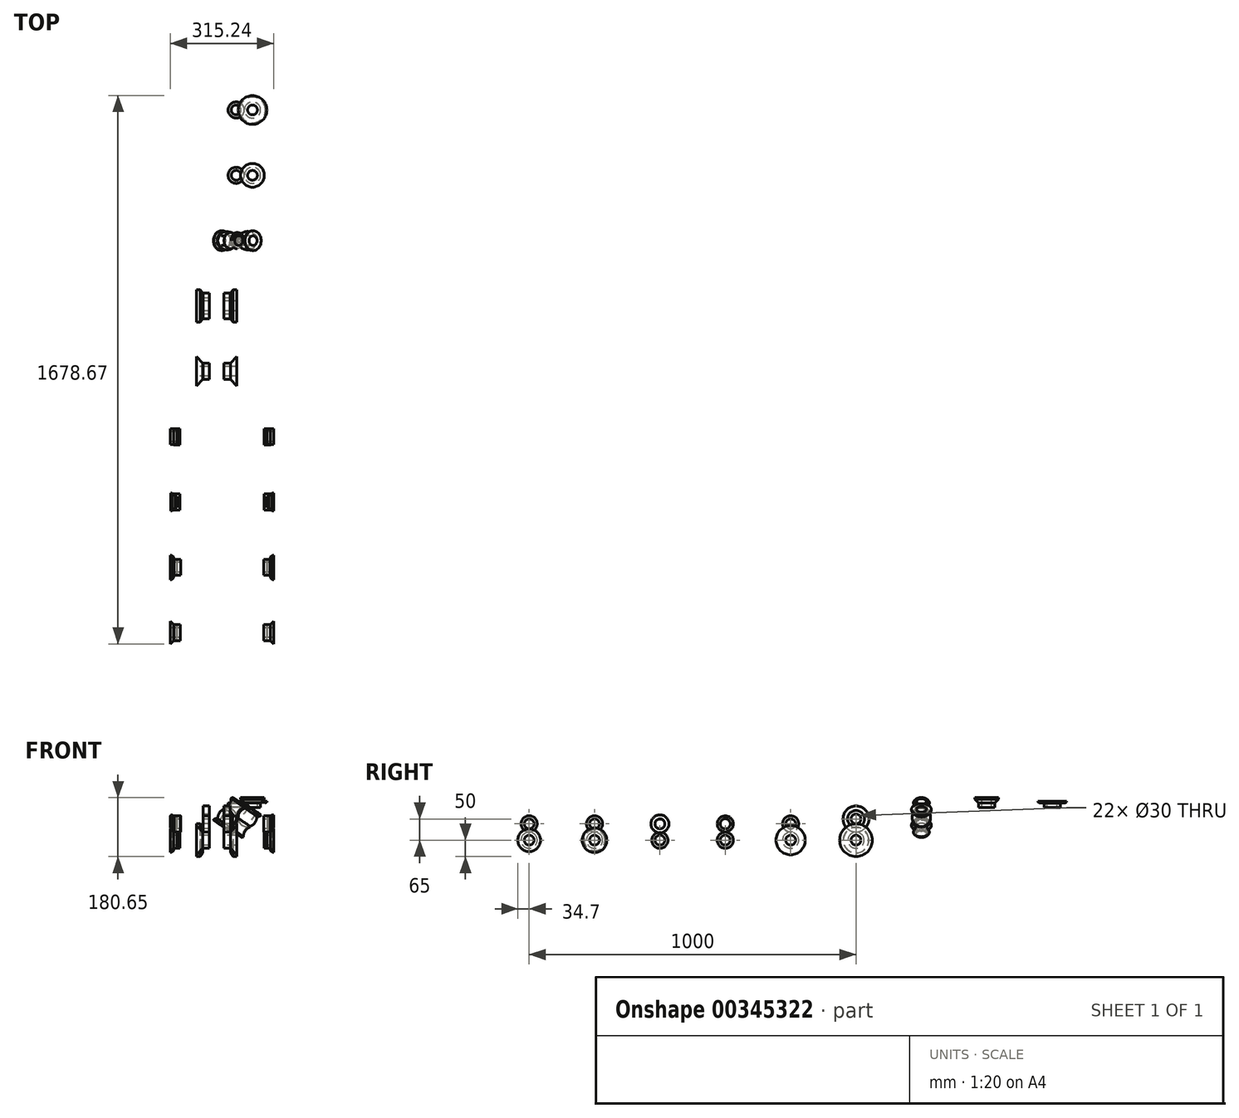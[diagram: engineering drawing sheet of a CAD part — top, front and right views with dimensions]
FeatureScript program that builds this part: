
annotation { "Feature Type Name" : "Feature", "Feature Type Description" : "" }
export const myFeature = defineFeature(function(context is Context, id is Id, definition is map)
    precondition{}
    {
        {
            var Q0;
            Q0=qCreatedBy(makeId("Front.planeOp"),FACE);
            var sketch = newSketch(context, id + "F0", { "sketchPlane" : qUnion([Q0])});
            skLineSegment(sketch, "E0", {"start": v(0, 0) * mm, "end": v(0, 89) * mm});
            skLineSegment(sketch, "E1", {"start": v(0, 0) * mm, "end": v(84, 0) * mm});
            skLineSegment(sketch, "E2", {"start": v(84, 0) * mm, "end": v(84, 14) * mm});
            skLineSegment(sketch, "E3", {"start": v(84, 14) * mm, "end": v(127, 75) * mm, "construction": true});
            skLineSegment(sketch, "E4", {"start": v(127, 75) * mm, "end": v(127, 89) * mm});
            skLineSegment(sketch, "E5", {"start": v(127, 89) * mm, "end": v(113, 89) * mm});
            skArc(sketch, "E6", {"start": v(84, 14) * mm, "mid": v(100.07, 25.5) * mm, "end": v(105.5, 44.5) * mm});
            skArc(sketch, "E7", {"start": v(127, 75) * mm, "mid": v(110.93, 63.5) * mm, "end": v(105.5, 44.5) * mm});
            skLineSegment(sketch, "E8", {"start": v(0, 89) * mm, "end": v(2, 89) * mm});
            skLineSegment(sketch, "E9", {"start": v(2, 89) * mm, "end": v(2, 83) * mm});
            skLineSegment(sketch, "E10", {"start": v(113, 89) * mm, "end": v(113, 87) * mm});
            skLineSegment(sketch, "E11", {"start": v(113, 87) * mm, "end": v(119, 87) * mm});
            skSolve(sketch);
        }
        {
            var Q0;
            Q0=qCreatedBy(makeId("Front.planeOp"),FACE);
            cPlane(context, id + "F1", {"entities" : qUnion([Q0]), "cplaneType" : CPlaneType.OFFSET, "offset" : 200 * mm, "oppositeDirection" : true, "width" : 150 * mm, "height" : 150 * mm});
        }
        {
            var Q0;
            Q0=qCreatedBy(id+"F1.planeOp",FACE);
            cPlane(context, id + "F2", {"entities" : qUnion([Q0]), "cplaneType" : CPlaneType.OFFSET, "offset" : 200 * mm, "oppositeDirection" : true, "width" : 150 * mm, "height" : 150 * mm});
        }
        {
            var Q0;
            Q0=qCreatedBy(id+"F2.planeOp",FACE);
            cPlane(context, id + "F3", {"entities" : qUnion([Q0]), "cplaneType" : CPlaneType.OFFSET, "offset" : 200 * mm, "oppositeDirection" : true, "width" : 150 * mm, "height" : 150 * mm});
        }
        {
            var Q0;
            Q0=qCreatedBy(id+"F3.planeOp",FACE);
            cPlane(context, id + "F4", {"entities" : qUnion([Q0]), "cplaneType" : CPlaneType.OFFSET, "offset" : 200 * mm, "oppositeDirection" : true, "width" : 150 * mm, "height" : 150 * mm});
        }
        {
            var Q0;
            Q0=qCreatedBy(id+"F4.planeOp",FACE);
            cPlane(context, id + "F5", {"entities" : qUnion([Q0]), "cplaneType" : CPlaneType.OFFSET, "offset" : 200 * mm, "oppositeDirection" : true, "width" : 150 * mm, "height" : 150 * mm});
        }
        {
            var Q0;
            Q0=qCreatedBy(id+"F5.planeOp",FACE);
            cPlane(context, id + "F6", {"entities" : qUnion([Q0]), "cplaneType" : CPlaneType.OFFSET, "offset" : 200 * mm, "oppositeDirection" : true, "width" : 150 * mm, "height" : 150 * mm});
        }
        {
            var Q0;
            Q0=qCreatedBy(id+"F6.planeOp",FACE);
            cPlane(context, id + "F7", {"entities" : qUnion([Q0]), "cplaneType" : CPlaneType.OFFSET, "offset" : 200 * mm, "oppositeDirection" : true, "width" : 150 * mm, "height" : 150 * mm});
        }
        {
            var Q0;
            Q0=qCreatedBy(id+"F7.planeOp",FACE);
            cPlane(context, id + "F8", {"entities" : qUnion([Q0]), "cplaneType" : CPlaneType.OFFSET, "offset" : 200 * mm, "oppositeDirection" : true, "width" : 150 * mm, "height" : 150 * mm});
        }
        {
            var Q0;
            Q0=qCreatedBy(id+"F8.planeOp",FACE);
            cPlane(context, id + "F9", {"entities" : qUnion([Q0]), "cplaneType" : CPlaneType.OFFSET, "offset" : 200 * mm, "oppositeDirection" : true, "width" : 150 * mm, "height" : 150 * mm});
        }
        {
            var Q0;
            Q0=qCreatedBy(id+"F9.planeOp",FACE);
            cPlane(context, id + "F10", {"entities" : qUnion([Q0]), "cplaneType" : CPlaneType.OFFSET, "offset" : 200 * mm, "oppositeDirection" : true, "width" : 150 * mm, "height" : 150 * mm});
        }
        {
            var Q0;
            Q0=qCreatedBy(id+"F1.planeOp",FACE);
            var sketch = newSketch(context, id + "F11", { "sketchPlane" : qUnion([Q0])});
            skLineSegment(sketch, "E12", {"start": v(0, 0) * mm, "end": v(206, 0) * mm});
            skLineSegment(sketch, "E13", {"start": v(0, 0) * mm, "end": v(-89, 0) * mm});
            skLineSegment(sketch, "E14", {"start": v(206, 0) * mm, "end": v(210.24, 4.24) * mm});
            skLineSegment(sketch, "E15", {"start": v(-89, 0) * mm, "end": v(-93.95, 4.95) * mm});
            skLineSegment(sketch, "E16.0", {"start": v(206.12, -0.3) * mm, "end": v(210.45, 4.03) * mm});
            skLineSegment(sketch, "E16.1", {"start": v(0, -0.3) * mm, "end": v(206.12, -0.3) * mm});
            skLineSegment(sketch, "E16.2", {"start": v(0, -0.3) * mm, "end": v(-89.12, -0.3) * mm});
            skLineSegment(sketch, "E16.3", {"start": v(-89.12, -0.3) * mm, "end": v(-94.16, 4.74) * mm});
            skLineSegment(sketch, "E17.0", {"start": v(205.88, 0.3) * mm, "end": v(210.03, 4.45) * mm});
            skLineSegment(sketch, "E17.1", {"start": v(0, 0.3) * mm, "end": v(205.88, 0.3) * mm});
            skLineSegment(sketch, "E17.2", {"start": v(0, 0.3) * mm, "end": v(-88.88, 0.3) * mm});
            skLineSegment(sketch, "E17.3", {"start": v(-88.88, 0.3) * mm, "end": v(-93.74, 5.16) * mm});
            skLineSegment(sketch, "E18", {"start": v(196.12, -0.3) * mm, "end": v(196.12, -10) * mm});
            skLineSegment(sketch, "E19", {"start": v(196.12, -10) * mm, "end": v(216.12, -10) * mm});
            skLineSegment(sketch, "E20", {"start": v(216.12, -10) * mm, "end": v(216.12, 9.7) * mm});
            skLineSegment(sketch, "E21", {"start": v(210.45, 4.03) * mm, "end": v(216.12, 9.7) * mm});
            skLineSegment(sketch, "E22", {"start": v(173.5, -25) * mm, "end": v(227.83, -25) * mm, "construction": true});
            skLineSegment(sketch, "E23", {"start": v(185.88, 0.3) * mm, "end": v(185.88, 10) * mm});
            skLineSegment(sketch, "E24", {"start": v(185.88, 10) * mm, "end": v(205.88, 10) * mm});
            skLineSegment(sketch, "E25", {"start": v(205.88, 10) * mm, "end": v(205.88, 0.3) * mm});
            skLineSegment(sketch, "E26", {"start": v(171.99, 25) * mm, "end": v(230.7, 25) * mm, "construction": true});
            skLineSegment(sketch, "E27", {"start": v(58.5, 25.23) * mm, "end": v(58.5, -30.96) * mm, "construction": true});
            skLineSegment(sketch, "E28.MirrorCS", {"start": v(-68.88, 10) * mm, "end": v(-88.88, 10) * mm});
            skLineSegment(sketch, "E29.MirrorCS", {"start": v(-88.88, 10) * mm, "end": v(-88.88, 0.3) * mm});
            skLineSegment(sketch, "E30.MirrorCS", {"start": v(-68.88, 0.3) * mm, "end": v(-68.88, 10) * mm});
            skLineSegment(sketch, "E31.MirrorCS", {"start": v(-79.12, -0.3) * mm, "end": v(-79.12, -10) * mm});
            skLineSegment(sketch, "E32.MirrorCS", {"start": v(-79.12, -10) * mm, "end": v(-99.12, -10) * mm});
            skLineSegment(sketch, "E33.MirrorCS", {"start": v(-99.12, -10) * mm, "end": v(-99.12, 9.7) * mm});
            skLineSegment(sketch, "E34.MirrorCS", {"start": v(-93.45, 4.03) * mm, "end": v(-99.12, 9.7) * mm});
            skSolve(sketch);
        }
        {
            var Q0;
            Q0=qCreatedBy(id+"F2.planeOp",FACE);
            var sketch = newSketch(context, id + "F12", { "sketchPlane" : qUnion([Q0])});
            skLineSegment(sketch, "E35.0", {"start": v(171.99, 25) * mm, "end": v(230.7, 25) * mm, "construction": true});
            skLineSegment(sketch, "E36.0", {"start": v(173.5, -25) * mm, "end": v(227.83, -25) * mm, "construction": true});
            skLineSegment(sketch, "E37.0", {"start": v(196.12, -0.3) * mm, "end": v(196.12, -10) * mm});
            skLineSegment(sketch, "E38", {"start": v(196.12, -0.3) * mm, "end": v(206.12, -0.3) * mm});
            skLineSegment(sketch, "E39", {"start": v(206.12, -0.3) * mm, "end": v(206.12, 6.7) * mm});
            skLineSegment(sketch, "E40", {"start": v(206.12, 6.7) * mm, "end": v(213.12, 12.5) * mm});
            skLineSegment(sketch, "E41.0", {"start": v(196.12, -10) * mm, "end": v(216.12, -10) * mm});
            skPoint(sketch, "E42.orphan", {"position": v(208.77, 12.5) * mm});
            skLineSegment(sketch, "E43.bottom", {"start": v(205.52, 0.3) * mm, "end": v(185.52, 0.3) * mm});
            skLineSegment(sketch, "E43.top", {"start": v(205.52, 10) * mm, "end": v(185.52, 10) * mm});
            skLineSegment(sketch, "E43.left", {"start": v(205.52, 0.3) * mm, "end": v(205.52, 10) * mm});
            skLineSegment(sketch, "E43.right", {"start": v(185.52, 0.3) * mm, "end": v(185.52, 10) * mm});
            skLineSegment(sketch, "E44", {"start": v(216.12, -10) * mm, "end": v(216.12, 12.5) * mm});
            skLineSegment(sketch, "E45", {"start": v(213.12, 12.5) * mm, "end": v(216.12, 12.5) * mm});
            skLineSegment(sketch, "E46.1", {"start": v(205.82, 0) * mm, "end": v(205.82, 6) * mm});
            skLineSegment(sketch, "E47", {"start": v(205.82, 0) * mm, "end": v(0, 0) * mm});
            skLineSegment(sketch, "E48.0", {"start": v(58.5, 25.23) * mm, "end": v(58.5, -30.96) * mm, "construction": true});
            skLineSegment(sketch, "E49.MirrorCS", {"start": v(-99.12, -10) * mm, "end": v(-99.12, 12.5) * mm});
            skLineSegment(sketch, "E50.MirrorCS", {"start": v(-79.12, -10) * mm, "end": v(-99.12, -10) * mm});
            skLineSegment(sketch, "E51.MirrorCS", {"start": v(-79.12, -0.3) * mm, "end": v(-79.12, -10) * mm});
            skLineSegment(sketch, "E52.MirrorCS", {"start": v(-79.12, -0.3) * mm, "end": v(-89.12, -0.3) * mm});
            skLineSegment(sketch, "E53.MirrorCS", {"start": v(-89.12, -0.3) * mm, "end": v(-89.12, 6.7) * mm});
            skLineSegment(sketch, "E54.MirrorCS", {"start": v(-89.12, 6.7) * mm, "end": v(-96.12, 12.5) * mm});
            skLineSegment(sketch, "E55.MirrorCS", {"start": v(-88.52, 10) * mm, "end": v(-68.52, 10) * mm});
            skLineSegment(sketch, "E56.MirrorCS", {"start": v(-88.52, 0.3) * mm, "end": v(-88.52, 10) * mm});
            skLineSegment(sketch, "E57.MirrorCS", {"start": v(-88.52, 0.3) * mm, "end": v(-68.52, 0.3) * mm});
            skLineSegment(sketch, "E58.MirrorCS", {"start": v(-68.52, 0.3) * mm, "end": v(-68.52, 10) * mm});
            skLineSegment(sketch, "E59.MirrorCS", {"start": v(-96.12, 12.5) * mm, "end": v(-99.12, 12.5) * mm});
            skLineSegment(sketch, "E60.MirrorCS", {"start": v(-88.82, 0) * mm, "end": v(-88.82, 6) * mm});
            skLineSegment(sketch, "E61", {"start": v(-88.82, 0) * mm, "end": v(0, 0) * mm});
            skSolve(sketch);
        }
        {
            var Q0;
            Q0=qCreatedBy(id+"F3.planeOp",FACE);
            var sketch = newSketch(context, id + "F13", { "sketchPlane" : qUnion([Q0])});
            skLineSegment(sketch, "E62", {"start": v(211.05, -2.5) * mm, "end": v(201.05, 7.5) * mm});
            skLineSegment(sketch, "E63", {"start": v(211.05, -2.5) * mm, "end": v(216.05, -2.5) * mm});
            skLineSegment(sketch, "E64", {"start": v(216.05, -2.5) * mm, "end": v(216.05, 10) * mm});
            skLineSegment(sketch, "E65", {"start": v(216.05, 10) * mm, "end": v(196.05, 10) * mm});
            skLineSegment(sketch, "E66", {"start": v(196.05, 10) * mm, "end": v(196.05, 7.5) * mm});
            skLineSegment(sketch, "E67", {"start": v(196.05, 7.5) * mm, "end": v(201.05, 7.5) * mm});
            skLineSegment(sketch, "E68.0", {"start": v(171.99, 25) * mm, "end": v(230.7, 25) * mm, "construction": true});
            skLineSegment(sketch, "E69.0", {"start": v(173.5, -25) * mm, "end": v(227.83, -25) * mm, "construction": true});
            skLineSegment(sketch, "E70.bottom", {"start": v(187.12, -10) * mm, "end": v(207.12, -10) * mm});
            skLineSegment(sketch, "E70.top", {"start": v(187.12, -0.3) * mm, "end": v(207.12, -0.3) * mm});
            skLineSegment(sketch, "E70.left", {"start": v(187.12, -10) * mm, "end": v(187.12, -0.3) * mm});
            skLineSegment(sketch, "E70.right", {"start": v(207.12, -10) * mm, "end": v(207.12, -0.3) * mm});
            skLineSegment(sketch, "E71.0", {"start": v(-88.82, 0) * mm, "end": v(0, 0) * mm});
            skLineSegment(sketch, "E72.0", {"start": v(205.82, 0) * mm, "end": v(0, 0) * mm});
            skLineSegment(sketch, "E73", {"start": v(205.82, 0) * mm, "end": v(202.85, 5.2) * mm});
            skLineSegment(sketch, "E74.0", {"start": v(58.5, 25.23) * mm, "end": v(58.5, -30.96) * mm, "construction": true});
            skLineSegment(sketch, "E75.MirrorCS", {"start": v(-88.82, 0) * mm, "end": v(-85.85, 5.2) * mm});
            skLineSegment(sketch, "E76.MirrorCS", {"start": v(-94.05, -2.5) * mm, "end": v(-84.05, 7.5) * mm});
            skLineSegment(sketch, "E77.MirrorCS", {"start": v(-79.05, 7.5) * mm, "end": v(-84.05, 7.5) * mm});
            skLineSegment(sketch, "E78.MirrorCS", {"start": v(-79.05, 10) * mm, "end": v(-79.05, 7.5) * mm});
            skLineSegment(sketch, "E79.MirrorCS", {"start": v(-99.05, 10) * mm, "end": v(-79.05, 10) * mm});
            skLineSegment(sketch, "E80.MirrorCS", {"start": v(-99.05, -2.5) * mm, "end": v(-99.05, 10) * mm});
            skLineSegment(sketch, "E81.MirrorCS", {"start": v(-94.05, -2.5) * mm, "end": v(-99.05, -2.5) * mm});
            skLineSegment(sketch, "E82.MirrorCS", {"start": v(-70.12, -0.3) * mm, "end": v(-90.12, -0.3) * mm});
            skLineSegment(sketch, "E83.MirrorCS", {"start": v(-90.12, -10) * mm, "end": v(-90.12, -0.3) * mm});
            skLineSegment(sketch, "E84.MirrorCS", {"start": v(-70.12, -10) * mm, "end": v(-90.12, -10) * mm});
            skLineSegment(sketch, "E85.MirrorCS", {"start": v(-70.12, -10) * mm, "end": v(-70.12, -0.3) * mm});
            skSolve(sketch);
        }
        {
            var Q0;
            Q0=qCreatedBy(id+"F4.planeOp",FACE);
            var sketch = newSketch(context, id + "F14", { "sketchPlane" : qUnion([Q0])});
            skLineSegment(sketch, "E86.0", {"start": v(207.12, -10) * mm, "end": v(207.12, -0.3) * mm});
            skLineSegment(sketch, "E87.0", {"start": v(187.12, -0.3) * mm, "end": v(207.12, -0.3) * mm});
            skLineSegment(sketch, "E88.0", {"start": v(187.12, -10) * mm, "end": v(187.12, -0.3) * mm});
            skLineSegment(sketch, "E89.0", {"start": v(187.12, -10) * mm, "end": v(207.12, -10) * mm});
            skLineSegment(sketch, "E90.0", {"start": v(171.99, 25) * mm, "end": v(230.7, 25) * mm, "construction": true});
            skLineSegment(sketch, "E91.0", {"start": v(173.5, -25) * mm, "end": v(227.83, -25) * mm, "construction": true});
            skLineSegment(sketch, "E92", {"start": v(196.08, 2.3) * mm, "end": v(196.08, 9.55) * mm});
            skLineSegment(sketch, "E93", {"start": v(196.08, 9.55) * mm, "end": v(216.08, 9.55) * mm});
            skLineSegment(sketch, "E94", {"start": v(216.08, 9.55) * mm, "end": v(216.08, 0.5) * mm});
            skLineSegment(sketch, "E95.0", {"start": v(-88.82, 0) * mm, "end": v(0, 0) * mm});
            skLineSegment(sketch, "E96.0", {"start": v(205.82, 0) * mm, "end": v(0, 0) * mm});
            skLineSegment(sketch, "E97.0", {"start": v(58.5, 25.23) * mm, "end": v(58.5, -30.96) * mm, "construction": true});
            skLineSegment(sketch, "E98", {"start": v(205.82, 0) * mm, "end": v(205.82, 2) * mm});
            skLineSegment(sketch, "E99", {"start": v(205.82, 2) * mm, "end": v(199.75, 2) * mm});
            skLineSegment(sketch, "E100.0", {"start": v(205.52, 1.7) * mm, "end": v(199.75, 1.7) * mm});
            skLineSegment(sketch, "E100.1", {"start": v(205.52, 0.3) * mm, "end": v(205.52, 1.7) * mm});
            skLineSegment(sketch, "E100.2", {"start": v(205.52, 0.3) * mm, "end": v(0, 0.3) * mm});
            skLineSegment(sketch, "E101.1", {"start": v(206.12, 0) * mm, "end": v(206.12, 2.3) * mm});
            skLineSegment(sketch, "E102", {"start": v(216.08, 0.5) * mm, "end": v(206.58, 0.5) * mm});
            skLineSegment(sketch, "E103", {"start": v(206.58, 0.5) * mm, "end": v(206.58, 2.3) * mm});
            skLineSegment(sketch, "E104", {"start": v(206.58, 2.3) * mm, "end": v(196.08, 2.3) * mm});
            skLineSegment(sketch, "E105.MirrorCS", {"start": v(-79.08, 2.3) * mm, "end": v(-79.08, 9.55) * mm});
            skLineSegment(sketch, "E106.MirrorCS", {"start": v(-79.08, 9.55) * mm, "end": v(-99.08, 9.55) * mm});
            skLineSegment(sketch, "E107.MirrorCS", {"start": v(-89.58, 2.3) * mm, "end": v(-79.08, 2.3) * mm});
            skLineSegment(sketch, "E108.MirrorCS", {"start": v(-89.58, 0.5) * mm, "end": v(-89.58, 2.3) * mm});
            skLineSegment(sketch, "E109.MirrorCS", {"start": v(-99.08, 0.5) * mm, "end": v(-89.58, 0.5) * mm});
            skLineSegment(sketch, "E110.MirrorCS", {"start": v(-99.08, 9.55) * mm, "end": v(-99.08, 0.5) * mm});
            skLineSegment(sketch, "E111.MirrorCS", {"start": v(-90.12, -10) * mm, "end": v(-90.12, -0.3) * mm});
            skLineSegment(sketch, "E112.MirrorCS", {"start": v(-70.12, -0.3) * mm, "end": v(-90.12, -0.3) * mm});
            skLineSegment(sketch, "E113.MirrorCS", {"start": v(-70.12, -10) * mm, "end": v(-70.12, -0.3) * mm});
            skLineSegment(sketch, "E114.MirrorCS", {"start": v(-70.12, -10) * mm, "end": v(-90.12, -10) * mm});
            skLineSegment(sketch, "E115.MirrorCS", {"start": v(-88.82, 0) * mm, "end": v(-88.82, 2) * mm});
            skLineSegment(sketch, "E116.MirrorCS", {"start": v(-88.82, 2) * mm, "end": v(-82.75, 2) * mm});
            skSolve(sketch);
        }
        {
            var Q0;
            Q0=qCreatedBy(id+"F5.planeOp",FACE);
            var sketch = newSketch(context, id + "F15", { "sketchPlane" : qUnion([Q0])});
            skLineSegment(sketch, "E117", {"start": v(0, 0) * mm, "end": v(84, 0) * mm});
            skLineSegment(sketch, "E118", {"start": v(84, 0) * mm, "end": v(174.5, 90.5) * mm});
            skLineSegment(sketch, "E119", {"start": v(0, 0) * mm, "end": v(-62.93, 62.93) * mm});
            skLineSegment(sketch, "E120.0", {"start": v(84.12, -0.3) * mm, "end": v(174.72, 90.3) * mm});
            skLineSegment(sketch, "E120.1", {"start": v(-0.12, -0.3) * mm, "end": v(84.12, -0.3) * mm});
            skLineSegment(sketch, "E120.2", {"start": v(-0.12, -0.3) * mm, "end": v(-63.14, 62.72) * mm});
            skLineSegment(sketch, "E121.0", {"start": v(0.12, 0.3) * mm, "end": v(-62.72, 63.14) * mm});
            skLineSegment(sketch, "E121.1", {"start": v(0.12, 0.3) * mm, "end": v(83.88, 0.3) * mm});
            skLineSegment(sketch, "E121.2", {"start": v(83.88, 0.3) * mm, "end": v(174.3, 90.72) * mm});
            skLineSegment(sketch, "E122", {"start": v(64.12, -0.3) * mm, "end": v(64.12, -10) * mm});
            skLineSegment(sketch, "E123", {"start": v(64.12, -10) * mm, "end": v(104.12, -10) * mm});
            skLineSegment(sketch, "E124", {"start": v(104.12, -10) * mm, "end": v(104.12, 19.7) * mm});
            skLineSegment(sketch, "E125.0", {"start": v(173.5, -25) * mm, "end": v(227.83, -25) * mm, "construction": true});
            skLineSegment(sketch, "E126.0", {"start": v(171.99, 25) * mm, "end": v(230.7, 25) * mm, "construction": true});
            skLineSegment(sketch, "E127.bottom", {"start": v(63.88, 10) * mm, "end": v(83.88, 10) * mm});
            skLineSegment(sketch, "E127.top", {"start": v(63.88, 0.3) * mm, "end": v(83.88, 0.3) * mm});
            skLineSegment(sketch, "E127.left", {"start": v(63.88, 10) * mm, "end": v(63.88, 0.3) * mm});
            skLineSegment(sketch, "E127.right", {"start": v(83.88, 10) * mm, "end": v(83.88, 0.3) * mm});
            skLineSegment(sketch, "E128", {"start": v(42, 25.3) * mm, "end": v(42, -15.52) * mm, "construction": true});
            skLineSegment(sketch, "E129.MirrorCS", {"start": v(20.12, 10) * mm, "end": v(20.12, 0.3) * mm});
            skLineSegment(sketch, "E130.MirrorCS", {"start": v(20.12, 10) * mm, "end": v(0.12, 10) * mm});
            skLineSegment(sketch, "E131.MirrorCS", {"start": v(0.12, 10) * mm, "end": v(0.12, 0.3) * mm});
            skLineSegment(sketch, "E132.MirrorCS", {"start": v(19.88, -0.3) * mm, "end": v(19.88, -10) * mm});
            skLineSegment(sketch, "E133.MirrorCS", {"start": v(19.88, -10) * mm, "end": v(-20.12, -10) * mm});
            skLineSegment(sketch, "E134.MirrorCS", {"start": v(-20.12, -10) * mm, "end": v(-20.12, 19.7) * mm});
            skSolve(sketch);
        }
        {
            var Q0;
            Q0=qCreatedBy(id+"F6.planeOp",FACE);
            var sketch = newSketch(context, id + "F16", { "sketchPlane" : qUnion([Q0])});
            skLineSegment(sketch, "E135", {"start": v(0, 0) * mm, "end": v(83.7, 0) * mm});
            skLineSegment(sketch, "E136", {"start": v(83.7, 0) * mm, "end": v(83.7, 14) * mm});
            skLineSegment(sketch, "E137", {"start": v(83.7, 14) * mm, "end": v(149.41, 107.15) * mm});
            skLineSegment(sketch, "E138", {"start": v(0, 0) * mm, "end": v(0, 89) * mm});
            skLineSegment(sketch, "E139.0", {"start": v(84, 13.9) * mm, "end": v(149.66, 106.98) * mm});
            skLineSegment(sketch, "E139.1", {"start": v(84, -0.3) * mm, "end": v(84, 13.9) * mm});
            skLineSegment(sketch, "E139.2", {"start": v(-0.3, -0.3) * mm, "end": v(84, -0.3) * mm});
            skLineSegment(sketch, "E139.3", {"start": v(-0.3, -0.3) * mm, "end": v(-0.3, 89) * mm});
            skLineSegment(sketch, "E140.0", {"start": v(0.3, 0.3) * mm, "end": v(0.3, 89) * mm});
            skLineSegment(sketch, "E140.1", {"start": v(0.3, 0.3) * mm, "end": v(83.4, 0.3) * mm});
            skLineSegment(sketch, "E140.2", {"start": v(83.4, 0.3) * mm, "end": v(83.4, 14.1) * mm});
            skLineSegment(sketch, "E140.3", {"start": v(83.4, 14.1) * mm, "end": v(149.17, 107.33) * mm});
            skLineSegment(sketch, "E141", {"start": v(64, -0.3) * mm, "end": v(64, -10) * mm});
            skLineSegment(sketch, "E142", {"start": v(64, -10) * mm, "end": v(104, -10) * mm});
            skLineSegment(sketch, "E143", {"start": v(104, -10) * mm, "end": v(104, 25) * mm});
            skLineSegment(sketch, "E144", {"start": v(104, 25) * mm, "end": v(91.83, 25) * mm});
            skLineSegment(sketch, "E145.0", {"start": v(173.5, -25) * mm, "end": v(227.83, -25) * mm, "construction": true});
            skLineSegment(sketch, "E146", {"start": v(64.37, 0.3) * mm, "end": v(64.37, 25) * mm});
            skLineSegment(sketch, "E147", {"start": v(64.37, 25) * mm, "end": v(91.1, 25) * mm});
            skLineSegment(sketch, "E148", {"start": v(50.32, 40) * mm, "end": v(125.83, 40) * mm, "construction": true});
            skLineSegment(sketch, "E149", {"start": v(0.3, 25) * mm, "end": v(20.3, 25) * mm});
            skLineSegment(sketch, "E150", {"start": v(20.3, 25) * mm, "end": v(20.3, 0.3) * mm});
            skLineSegment(sketch, "E151.0", {"start": v(42, 25.3) * mm, "end": v(42, -15.52) * mm, "construction": true});
            skLineSegment(sketch, "E152.MirrorCS", {"start": v(20, -0.3) * mm, "end": v(20, -10) * mm});
            skLineSegment(sketch, "E153.MirrorCS", {"start": v(-20, -10) * mm, "end": v(-20, 25) * mm});
            skLineSegment(sketch, "E154.MirrorCS", {"start": v(20, -10) * mm, "end": v(-20, -10) * mm});
            skLineSegment(sketch, "E155.MirrorCS", {"start": v(-20, 25) * mm, "end": v(-7.83, 25) * mm});
            skLineSegment(sketch, "E156.MirrorCS", {"start": v(-0.3, 14.33) * mm, "end": v(-7.83, 25) * mm});
            skPoint(sketch, "E157.orphan", {"position": v(-65.66, 106.98) * mm});
            skPoint(sketch, "E158.orphan", {"position": v(0, 13.9) * mm});
            skSolve(sketch);
        }
        {
            var Q0;
            Q0=qCreatedBy(id+"F7.planeOp",FACE);
            var sketch = newSketch(context, id + "F17", { "sketchPlane" : qUnion([Q0])});
            skLineSegment(sketch, "E159", {"start": v(0, 0) * mm, "end": v(83.7, 0) * mm});
            skLineSegment(sketch, "E160", {"start": v(83.7, 0) * mm, "end": v(83.7, 14) * mm});
            skLineSegment(sketch, "E161", {"start": v(83.7, 14) * mm, "end": v(126.7, 75) * mm, "construction": true});
            skLineSegment(sketch, "E162", {"start": v(0, 0) * mm, "end": v(0, 89) * mm});
            skArc(sketch, "E163", {"start": v(83.7, 14) * mm, "mid": v(99.77, 25.5) * mm, "end": v(105.2, 44.5) * mm});
            skArc(sketch, "E164", {"start": v(126.7, 75) * mm, "mid": v(110.64, 63.5) * mm, "end": v(105.2, 44.5) * mm});
            skLineSegment(sketch, "E165", {"start": v(126.7, 75) * mm, "end": v(126.7, 109) * mm});
            skLineSegment(sketch, "E166.0", {"start": v(127, 74.77) * mm, "end": v(127, 109) * mm});
            skArc(sketch, "E166.1", {"start": v(127, 74.77) * mm, "mid": v(110.95, 63.41) * mm, "end": v(105.5, 44.51) * mm});
            skLineSegment(sketch, "E166.2", {"start": v(-0.3, -0.3) * mm, "end": v(-0.3, 77.26) * mm});
            skLineSegment(sketch, "E166.3", {"start": v(-0.3, -0.3) * mm, "end": v(84, -0.3) * mm});
            skLineSegment(sketch, "E166.4", {"start": v(84, -0.3) * mm, "end": v(84, 13.78) * mm});
            skArc(sketch, "E166.5", {"start": v(84, 13.78) * mm, "mid": v(100.08, 25.42) * mm, "end": v(105.5, 44.51) * mm});
            skLineSegment(sketch, "E167.0", {"start": v(126.4, 75.22) * mm, "end": v(126.4, 109) * mm});
            skArc(sketch, "E167.1", {"start": v(126.4, 75.22) * mm, "mid": v(110.33, 63.58) * mm, "end": v(104.9, 44.48) * mm});
            skLineSegment(sketch, "E167.2", {"start": v(0.3, 0.3) * mm, "end": v(0.3, 77.26) * mm});
            skLineSegment(sketch, "E167.3", {"start": v(0.3, 0.3) * mm, "end": v(83.4, 0.3) * mm});
            skLineSegment(sketch, "E167.4", {"start": v(83.4, 0.3) * mm, "end": v(83.4, 14.23) * mm});
            skArc(sketch, "E167.5", {"start": v(83.4, 14.23) * mm, "mid": v(99.46, 25.58) * mm, "end": v(104.9, 44.48) * mm});
            skLineSegment(sketch, "E168", {"start": v(141.21, 78.21) * mm, "end": v(88.99, 4.14) * mm});
            skLineSegment(sketch, "E169", {"start": v(88.99, 4.14) * mm, "end": v(84, 7.66) * mm});
            skLineSegment(sketch, "E170", {"start": v(89.66, -20.93) * mm, "end": v(174.5, 99.37) * mm, "construction": true});
            skLineSegment(sketch, "E171", {"start": v(127, 84.65) * mm, "end": v(128.7, 87.04) * mm});
            skLineSegment(sketch, "E172", {"start": v(128.7, 87.04) * mm, "end": v(141.21, 78.21) * mm});
            skLineSegment(sketch, "E173.1.0", {"start": v(83.4, 4.34) * mm, "end": v(81.72, 1.95) * mm});
            skLineSegment(sketch, "E173.1.1", {"start": v(81.72, 1.95) * mm, "end": v(69.2, 10.78) * mm});
            skLineSegment(sketch, "E173.1.2", {"start": v(69.2, 10.78) * mm, "end": v(121.42, 84.85) * mm});
            skLineSegment(sketch, "E173.1.3", {"start": v(121.42, 84.85) * mm, "end": v(126.4, 81.33) * mm});
            skPoint(sketch, "E173.center", {"position": v(105.2, 44.5) * mm});
            skLineSegment(sketch, "E173.anchor1", {"start": v(105.2, 44.5) * mm, "end": v(127, 84.65) * mm, "construction": true});
            skLineSegment(sketch, "E173.anchor2", {"start": v(105.2, 44.5) * mm, "end": v(83.4, 4.34) * mm, "construction": true});
            skLineSegment(sketch, "E174.MirrorCS", {"start": v(48.8, 7.89) * mm, "end": v(133.63, 128.19) * mm, "construction": true});
            skSolve(sketch);
        }
        {
            var Q0;
            Q0=qCreatedBy(id+"F8.planeOp",FACE);
            var sketch = newSketch(context, id + "F18", { "sketchPlane" : qUnion([Q0])});
            skLineSegment(sketch, "E175", {"start": v(126.7, 75) * mm, "end": v(126.7, 89) * mm});
            skLineSegment(sketch, "E176", {"start": v(126.7, 89) * mm, "end": v(116.81, 98.9) * mm});
            skLineSegment(sketch, "E177.1", {"start": v(127, 89.12) * mm, "end": v(115.41, 100.72) * mm});
            skLineSegment(sketch, "E177.2", {"start": v(127, 75) * mm, "end": v(127, 89.12) * mm});
            skLineSegment(sketch, "E178.1", {"start": v(126.4, 88.87) * mm, "end": v(116.81, 98.47) * mm});
            skLineSegment(sketch, "E178.2", {"start": v(126.4, 75.87) * mm, "end": v(126.4, 88.87) * mm});
            skLineSegment(sketch, "E179", {"start": v(126.4, 88.87) * mm, "end": v(116.7, 88.87) * mm});
            skLineSegment(sketch, "E180", {"start": v(116.7, 88.87) * mm, "end": v(116.7, 75.87) * mm});
            skLineSegment(sketch, "E181", {"start": v(116.7, 75.87) * mm, "end": v(126.4, 75.87) * mm});
            skLineSegment(sketch, "E182", {"start": v(101.7, 117.95) * mm, "end": v(101.7, 62.03) * mm, "construction": true});
            skLineSegment(sketch, "E183", {"start": v(151.7, 118.79) * mm, "end": v(151.7, 53.17) * mm, "construction": true});
            skLineSegment(sketch, "E184", {"start": v(127, 75) * mm, "end": v(136.7, 75) * mm});
            skLineSegment(sketch, "E185", {"start": v(136.7, 75) * mm, "end": v(136.7, 105.55) * mm});
            skLineSegment(sketch, "E186", {"start": v(136.7, 105.55) * mm, "end": v(115.41, 105.55) * mm});
            skLineSegment(sketch, "E187", {"start": v(115.41, 100.72) * mm, "end": v(115.41, 105.55) * mm});
            skArc(sketch, "E188.0", {"start": v(126.7, 75) * mm, "mid": v(110.64, 63.5) * mm, "end": v(105.2, 44.5) * mm});
            skArc(sketch, "E189.0", {"start": v(126.4, 75.22) * mm, "mid": v(110.33, 63.58) * mm, "end": v(104.9, 44.48) * mm});
            skArc(sketch, "E190.0", {"start": v(127, 74.77) * mm, "mid": v(110.95, 63.41) * mm, "end": v(105.5, 44.51) * mm});
            skArc(sketch, "E191.0", {"start": v(83.4, 14.23) * mm, "mid": v(99.46, 25.58) * mm, "end": v(104.9, 44.48) * mm});
            skArc(sketch, "E192.0", {"start": v(83.7, 14) * mm, "mid": v(99.77, 25.5) * mm, "end": v(105.2, 44.5) * mm});
            skArc(sketch, "E193.0", {"start": v(84, 13.78) * mm, "mid": v(100.08, 25.42) * mm, "end": v(105.5, 44.51) * mm});
            skLineSegment(sketch, "E194.0", {"start": v(83.4, 0.3) * mm, "end": v(83.4, 14.23) * mm});
            skLineSegment(sketch, "E195.0", {"start": v(84, -0.3) * mm, "end": v(84, 13.78) * mm});
            skLineSegment(sketch, "E196.0", {"start": v(0.3, 0.3) * mm, "end": v(83.4, 0.3) * mm});
            skLineSegment(sketch, "E197.0", {"start": v(-0.3, -0.3) * mm, "end": v(84, -0.3) * mm});
            skLineSegment(sketch, "E198.0", {"start": v(0, 0) * mm, "end": v(83.7, 0) * mm});
            skLineSegment(sketch, "E199.0", {"start": v(0.3, 0.3) * mm, "end": v(0.3, 77.26) * mm});
            skLineSegment(sketch, "E200.0", {"start": v(-0.3, -0.3) * mm, "end": v(-0.3, 77.26) * mm});
            skLineSegment(sketch, "E201", {"start": v(116.81, 98.9) * mm, "end": v(115.4, 97.48) * mm});
            skLineSegment(sketch, "E202", {"start": v(115.4, 97.48) * mm, "end": v(118.87, 94) * mm});
            skLineSegment(sketch, "E203.0", {"start": v(114.97, 97.48) * mm, "end": v(118.66, 93.8) * mm});
            skLineSegment(sketch, "E203.1", {"start": v(116.81, 99.32) * mm, "end": v(114.97, 97.48) * mm});
            skLineSegment(sketch, "E204.0", {"start": v(115.82, 97.48) * mm, "end": v(119.08, 94.22) * mm});
            skLineSegment(sketch, "E204.1", {"start": v(116.81, 98.47) * mm, "end": v(115.82, 97.48) * mm});
            skSolve(sketch);
        }
        {
            var Q0;
            Q0=qCreatedBy(id+"F9.planeOp",FACE);
            var sketch = newSketch(context, id + "F19", { "sketchPlane" : qUnion([Q0])});
            skLineSegment(sketch, "E205", {"start": v(127, 75.43) * mm, "end": v(127, 89.12) * mm});
            skLineSegment(sketch, "E206", {"start": v(127, 89.12) * mm, "end": v(112.23, 89.12) * mm});
            skLineSegment(sketch, "E207", {"start": v(107.74, 94.58) * mm, "end": v(136.7, 94.58) * mm});
            skLineSegment(sketch, "E208", {"start": v(136.7, 94.58) * mm, "end": v(136.7, 75.43) * mm});
            skLineSegment(sketch, "E209", {"start": v(136.7, 75.43) * mm, "end": v(127, 75.43) * mm});
            skLineSegment(sketch, "E210.0", {"start": v(127, 75) * mm, "end": v(127, 89.12) * mm});
            skLineSegment(sketch, "E211", {"start": v(127, 89.12) * mm, "end": v(113, 89.12) * mm});
            skLineSegment(sketch, "E212.0", {"start": v(101.7, 117.95) * mm, "end": v(101.7, 62.03) * mm, "construction": true});
            skLineSegment(sketch, "E213.0", {"start": v(151.7, 118.79) * mm, "end": v(151.7, 53.17) * mm, "construction": true});
            skLineSegment(sketch, "E214", {"start": v(126.4, 75.87) * mm, "end": v(116.7, 75.87) * mm});
            skLineSegment(sketch, "E215", {"start": v(116.7, 75.87) * mm, "end": v(116.7, 86.52) * mm});
            skLineSegment(sketch, "E216", {"start": v(112.23, 89.12) * mm, "end": v(107.74, 92.05) * mm});
            skLineSegment(sketch, "E217", {"start": v(107.74, 92.05) * mm, "end": v(107.74, 94.58) * mm});
            skArc(sketch, "E218.0", {"start": v(126.4, 75.22) * mm, "mid": v(110.33, 63.58) * mm, "end": v(104.9, 44.48) * mm});
            skArc(sketch, "E219.0", {"start": v(126.7, 75) * mm, "mid": v(110.64, 63.5) * mm, "end": v(105.2, 44.5) * mm});
            skArc(sketch, "E220.0", {"start": v(127, 74.77) * mm, "mid": v(110.95, 63.41) * mm, "end": v(105.5, 44.51) * mm});
            skLineSegment(sketch, "E221", {"start": v(113, 89.12) * mm, "end": v(113, 86.52) * mm});
            skLineSegment(sketch, "E222", {"start": v(113, 86.52) * mm, "end": v(126.4, 86.52) * mm});
            skLineSegment(sketch, "E223", {"start": v(126.4, 75.22) * mm, "end": v(126.4, 88.52) * mm});
            skLineSegment(sketch, "E224.0", {"start": v(113.6, 87.12) * mm, "end": v(118.04, 87.12) * mm});
            skLineSegment(sketch, "E224.1", {"start": v(113.6, 88.52) * mm, "end": v(113.6, 87.12) * mm});
            skLineSegment(sketch, "E224.2", {"start": v(126.4, 88.52) * mm, "end": v(113.6, 88.52) * mm});
            skSolve(sketch);
        }
        {
            var Q0;
            {var subQ2=sQuery(id+"F16.wireOp",EDGE,"E140.2");Q0=makeQuery(id+"F16.imprint","IMPRINT",FACE,{"disambiguationData":[TD([[makeQuery(id+"F16.imprint","IMPRINT",EDGE,{"derivedFrom":subQ2}),1.0]])]});}
            var Q1;
            Q1=sQuery(id+"F16.wireOp",EDGE,"E148");
            revolve(context, id + "F20", {"entities" : qUnion([Q0]), "axis" : qUnion([Q1]), "revolveType" : RevolveType.FULL});
        }
        {
            var Q0;
            {var subQ1=sQuery(id+"F16.wireOp",EDGE,"E139.1");Q0=makeQuery(id+"F16.imprint","IMPRINT",FACE,{"disambiguationData":[TD([[makeQuery(id+"F16.imprint","IMPRINT",EDGE,{"derivedFrom":subQ1}),-1.0]])]});}
            var Q1;
            Q1=sQuery(id+"F16.wireOp",EDGE,"E145.0");
            revolve(context, id + "F21", {"entities" : qUnion([Q0]), "axis" : qUnion([Q1]), "revolveType" : RevolveType.FULL});
        }
        {
            var Q0;
            Q0=makeQuery(id+"F11.imprint","IMPRINT",FACE,{"disambiguationData":[TD([[makeQuery(id+"F11.imprint","IMPRINT",EDGE,{"derivedFrom":sQuery(id+"F11.wireOp",EDGE,"E28.MirrorCS")}),1.0]])]});
            var Q1;
            {var subQ2=sQuery(id+"F11.wireOp",EDGE,"E23");Q1=makeQuery(id+"F11.imprint","IMPRINT",FACE,{"disambiguationData":[TD([[makeQuery(id+"F11.imprint","IMPRINT",EDGE,{"derivedFrom":subQ2}),-1.0]])]});}
            var Q2;
            Q2=sQuery(id+"F11.wireOp",EDGE,"E26");
            revolve(context, id + "F22", {"entities" : qUnion([Q0, Q1]), "axis" : qUnion([Q2]), "revolveType" : RevolveType.FULL});
        }
        {
            var Q0;
            {var subQ1=sQuery(id+"F11.wireOp",EDGE,"E16.3");Q0=makeQuery(id+"F11.imprint","IMPRINT",FACE,{"disambiguationData":[TD([[makeQuery(id+"F11.imprint","IMPRINT",EDGE,{"derivedFrom":subQ1}),1.0]])]});}
            var Q1;
            {var subQ2=sQuery(id+"F11.wireOp",EDGE,"E16.0");Q1=makeQuery(id+"F11.imprint","IMPRINT",FACE,{"disambiguationData":[TD([[makeQuery(id+"F11.imprint","IMPRINT",EDGE,{"derivedFrom":subQ2}),-1.0]])]});}
            var Q2;
            Q2=sQuery(id+"F11.wireOp",EDGE,"E22");
            revolve(context, id + "F23", {"entities" : qUnion([Q0, Q1]), "axis" : qUnion([Q2]), "revolveType" : RevolveType.FULL});
        }
        {
            var Q0;
            Q0=makeQuery(id+"F12.imprint","IMPRINT",FACE,{"disambiguationData":[TD([[makeQuery(id+"F12.imprint","IMPRINT",EDGE,{"derivedFrom":sQuery(id+"F12.wireOp",EDGE,"E55.MirrorCS")}),-1.0]])]});
            var Q1;
            Q1=makeQuery(id+"F12.imprint","IMPRINT",FACE,{"disambiguationData":[TD([[makeQuery(id+"F12.imprint","IMPRINT",EDGE,{"derivedFrom":sQuery(id+"F12.wireOp",EDGE,"E43.bottom")}),-1.0]])]});
            var Q2;
            Q2=sQuery(id+"F12.wireOp",EDGE,"E35.0");
            revolve(context, id + "F24", {"entities" : qUnion([Q0, Q1]), "axis" : qUnion([Q2]), "revolveType" : RevolveType.FULL});
        }
        {
            var Q0;
            Q0=makeQuery(id+"F12.imprint","IMPRINT",FACE,{"disambiguationData":[TD([[makeQuery(id+"F12.imprint","IMPRINT",EDGE,{"derivedFrom":sQuery(id+"F12.wireOp",EDGE,"E49.MirrorCS")}),-1.0]])]});
            var Q1;
            Q1=makeQuery(id+"F12.imprint","IMPRINT",FACE,{"disambiguationData":[TD([[makeQuery(id+"F12.imprint","IMPRINT",EDGE,{"derivedFrom":sQuery(id+"F12.wireOp",EDGE,"E37.0")}),1.0]])]});
            var Q2;
            Q2=sQuery(id+"F12.wireOp",EDGE,"E36.0");
            revolve(context, id + "F25", {"entities" : qUnion([Q0, Q1]), "axis" : qUnion([Q2]), "revolveType" : RevolveType.FULL});
        }
        {
            var Q0;
            Q0=makeQuery(id+"F13.imprint","IMPRINT",FACE,{"disambiguationData":[TD([[makeQuery(id+"F13.imprint","IMPRINT",EDGE,{"derivedFrom":sQuery(id+"F13.wireOp",EDGE,"E62")}),-1.0]])]});
            var Q1;
            Q1=makeQuery(id+"F13.imprint","IMPRINT",FACE,{"disambiguationData":[TD([[makeQuery(id+"F13.imprint","IMPRINT",EDGE,{"derivedFrom":sQuery(id+"F13.wireOp",EDGE,"E76.MirrorCS")}),1.0]])]});
            var Q2;
            Q2=sQuery(id+"F13.wireOp",EDGE,"E68.0");
            revolve(context, id + "F26", {"entities" : qUnion([Q0, Q1]), "axis" : qUnion([Q2]), "revolveType" : RevolveType.FULL});
        }
        {
            var Q0;
            Q0=makeQuery(id+"F13.imprint","IMPRINT",FACE,{"disambiguationData":[TD([[makeQuery(id+"F13.imprint","IMPRINT",EDGE,{"derivedFrom":sQuery(id+"F13.wireOp",EDGE,"E82.MirrorCS")}),1.0]])]});
            var Q1;
            Q1=makeQuery(id+"F13.imprint","IMPRINT",FACE,{"disambiguationData":[TD([[makeQuery(id+"F13.imprint","IMPRINT",EDGE,{"derivedFrom":sQuery(id+"F13.wireOp",EDGE,"E70.bottom")}),1.0]])]});
            var Q2;
            Q2=sQuery(id+"F13.wireOp",EDGE,"E69.0");
            revolve(context, id + "F27", {"entities" : qUnion([Q0, Q1]), "axis" : qUnion([Q2]), "revolveType" : RevolveType.FULL});
        }
        {
            var Q0;
            {var subQ0=sQuery(id+"F14.wireOp",EDGE,"E92");Q0=makeQuery(id+"F14.imprint","IMPRINT",FACE,{"disambiguationData":[TD([[makeQuery(id+"F14.imprint","IMPRINT",EDGE,{"derivedFrom":subQ0}),-1.0]])]});}
            var Q1;
            Q1=makeQuery(id+"F14.imprint","IMPRINT",FACE,{"disambiguationData":[TD([[makeQuery(id+"F14.imprint","IMPRINT",EDGE,{"derivedFrom":sQuery(id+"F14.wireOp",EDGE,"E105.MirrorCS")}),1.0]])]});
            var Q2;
            Q2=sQuery(id+"F14.wireOp",EDGE,"E90.0");
            revolve(context, id + "F28", {"entities" : qUnion([Q0, Q1]), "axis" : qUnion([Q2]), "revolveType" : RevolveType.FULL});
        }
        {
            var Q0;
            Q0=makeQuery(id+"F14.imprint","IMPRINT",FACE,{"disambiguationData":[TD([[makeQuery(id+"F14.imprint","IMPRINT",EDGE,{"derivedFrom":sQuery(id+"F14.wireOp",EDGE,"E86.0")}),1.0]])]});
            var Q1;
            Q1=makeQuery(id+"F14.imprint","IMPRINT",FACE,{"disambiguationData":[TD([[makeQuery(id+"F14.imprint","IMPRINT",EDGE,{"derivedFrom":sQuery(id+"F14.wireOp",EDGE,"E111.MirrorCS")}),-1.0]])]});
            var Q2;
            Q2=sQuery(id+"F14.wireOp",EDGE,"E91.0");
            revolve(context, id + "F29", {"entities" : qUnion([Q0, Q1]), "axis" : qUnion([Q2]), "revolveType" : RevolveType.FULL});
        }
        {
            var Q0;
            Q0=makeQuery(id+"F15.imprint","IMPRINT",FACE,{"disambiguationData":[TD([[makeQuery(id+"F15.imprint","IMPRINT",EDGE,{"derivedFrom":sQuery(id+"F15.wireOp",EDGE,"E127.bottom")}),-1.0]])]});
            var Q1;
            {var subQ2=sQuery(id+"F15.wireOp",EDGE,"E129.MirrorCS");Q1=makeQuery(id+"F15.imprint","IMPRINT",FACE,{"disambiguationData":[TD([[makeQuery(id+"F15.imprint","IMPRINT",EDGE,{"derivedFrom":subQ2}),-1.0]])]});}
            var Q2;
            Q2=sQuery(id+"F15.wireOp",EDGE,"E126.0");
            revolve(context, id + "F30", {"entities" : qUnion([Q0, Q1]), "axis" : qUnion([Q2]), "revolveType" : RevolveType.FULL});
        }
        {
            var Q0;
            {var subQ3=sQuery(id+"F15.wireOp",EDGE,"E122");Q0=makeQuery(id+"F15.imprint","IMPRINT",FACE,{"disambiguationData":[TD([[makeQuery(id+"F15.imprint","IMPRINT",EDGE,{"derivedFrom":subQ3}),1.0]])]});}
            var Q1;
            {var subQ0=sQuery(id+"F15.wireOp",EDGE,"E132.MirrorCS");Q1=makeQuery(id+"F15.imprint","IMPRINT",FACE,{"disambiguationData":[TD([[makeQuery(id+"F15.imprint","IMPRINT",EDGE,{"derivedFrom":subQ0}),-1.0]])]});}
            var Q2;
            Q2=sQuery(id+"F15.wireOp",EDGE,"E125.0");
            revolve(context, id + "F31", {"entities" : qUnion([Q0, Q1]), "axis" : qUnion([Q2]), "revolveType" : RevolveType.FULL});
        }
        {
            var Q0;
            {var subQ2=sQuery(id+"F16.wireOp",EDGE,"E140.2");Q0=makeQuery(id+"F16.imprint","IMPRINT",FACE,{"disambiguationData":[TD([[makeQuery(id+"F16.imprint","IMPRINT",EDGE,{"derivedFrom":subQ2}),1.0]])]});}
            var Q1;
            {var subQ3=sQuery(id+"F16.wireOp",EDGE,"E149");Q1=makeQuery(id+"F16.imprint","IMPRINT",FACE,{"disambiguationData":[TD([[makeQuery(id+"F16.imprint","IMPRINT",EDGE,{"derivedFrom":subQ3}),-1.0]])]});}
            var Q2;
            Q2=sQuery(id+"F16.wireOp",EDGE,"E148");
            revolve(context, id + "F32", {"entities" : qUnion([Q0, Q1]), "axis" : qUnion([Q2]), "revolveType" : RevolveType.FULL});
        }
        {
            var Q0;
            {var subQ0=sQuery(id+"F16.wireOp",EDGE,"E152.MirrorCS");Q0=makeQuery(id+"F16.imprint","IMPRINT",FACE,{"disambiguationData":[TD([[makeQuery(id+"F16.imprint","IMPRINT",EDGE,{"derivedFrom":subQ0}),-1.0]])]});}
            var Q1;
            {var subQ1=sQuery(id+"F16.wireOp",EDGE,"E139.1");Q1=makeQuery(id+"F16.imprint","IMPRINT",FACE,{"disambiguationData":[TD([[makeQuery(id+"F16.imprint","IMPRINT",EDGE,{"derivedFrom":subQ1}),-1.0]])]});}
            var Q2;
            Q2=sQuery(id+"F16.wireOp",EDGE,"E145.0");
            revolve(context, id + "F33", {"entities" : qUnion([Q0, Q1]), "axis" : qUnion([Q2]), "revolveType" : RevolveType.FULL});
        }
        {
            var Q0;
            {var subQ3=sQuery(id+"F17.wireOp",EDGE,"E167.1");Q0=makeQuery(id+"F17.imprint","IMPRINT",FACE,{"disambiguationData":[TD([[makeQuery(id+"F17.imprint","IMPRINT",EDGE,{"derivedFrom":subQ3}),-1.0]])]});}
            var Q1;
            Q1=sQuery(id+"F17.wireOp",EDGE,"E174.MirrorCS");
            revolve(context, id + "F34", {"entities" : qUnion([Q0]), "axis" : qUnion([Q1]), "revolveType" : RevolveType.FULL});
        }
        {
            var Q0;
            {var subQ3=sQuery(id+"F17.wireOp",EDGE,"E166.1");Q0=makeQuery(id+"F17.imprint","IMPRINT",FACE,{"disambiguationData":[TD([[makeQuery(id+"F17.imprint","IMPRINT",EDGE,{"derivedFrom":subQ3}),1.0]])]});}
            var Q1;
            Q1=sQuery(id+"F17.wireOp",EDGE,"E170");
            revolve(context, id + "F35", {"entities" : qUnion([Q0]), "axis" : qUnion([Q1]), "revolveType" : RevolveType.FULL});
        }
        {
            var Q0;
            {var subQ0=sQuery(id+"F18.wireOp",EDGE,"E177.2");Q0=makeQuery(id+"F18.imprint","IMPRINT",FACE,{"disambiguationData":[TD([[makeQuery(id+"F18.imprint","IMPRINT",EDGE,{"derivedFrom":subQ0}),-1.0]])]});}
            var Q1;
            Q1=sQuery(id+"F18.wireOp",EDGE,"E183");
            revolve(context, id + "F36", {"entities" : qUnion([Q0]), "axis" : qUnion([Q1]), "revolveType" : RevolveType.FULL});
        }
        {
            var Q0;
            Q0=makeQuery(id+"F18.imprint","IMPRINT",FACE,{"disambiguationData":[TD([[makeQuery(id+"F18.imprint","IMPRINT",EDGE,{"derivedFrom":sQuery(id+"F18.wireOp",EDGE,"E178.2")}),1.0]])]});
            var Q1;
            Q1=sQuery(id+"F18.wireOp",EDGE,"E182");
            revolve(context, id + "F37", {"entities" : qUnion([Q0]), "axis" : qUnion([Q1]), "revolveType" : RevolveType.FULL});
        }
        {
            var Q0;
            Q0=makeQuery(id+"F19.imprint","IMPRINT",FACE,{"disambiguationData":[TD([[makeQuery(id+"F19.imprint","IMPRINT",EDGE,{"derivedFrom":sQuery(id+"F19.wireOp",EDGE,"E206")}),-1.0]])]});
            var Q1;
            Q1=sQuery(id+"F19.wireOp",EDGE,"E213.0");
            revolve(context, id + "F38", {"entities" : qUnion([Q0]), "axis" : qUnion([Q1]), "revolveType" : RevolveType.FULL});
        }
        {
            var Q0;
            {var subQ0=sQuery(id+"F19.wireOp",EDGE,"E214");Q0=makeQuery(id+"F19.imprint","IMPRINT",FACE,{"disambiguationData":[TD([[makeQuery(id+"F19.imprint","IMPRINT",EDGE,{"derivedFrom":subQ0}),-1.0]])]});}
            var Q1;
            Q1=sQuery(id+"F19.wireOp",EDGE,"E212.0");
            revolve(context, id + "F39", {"entities" : qUnion([Q0]), "axis" : qUnion([Q1]), "revolveType" : RevolveType.FULL});
        }
    });
